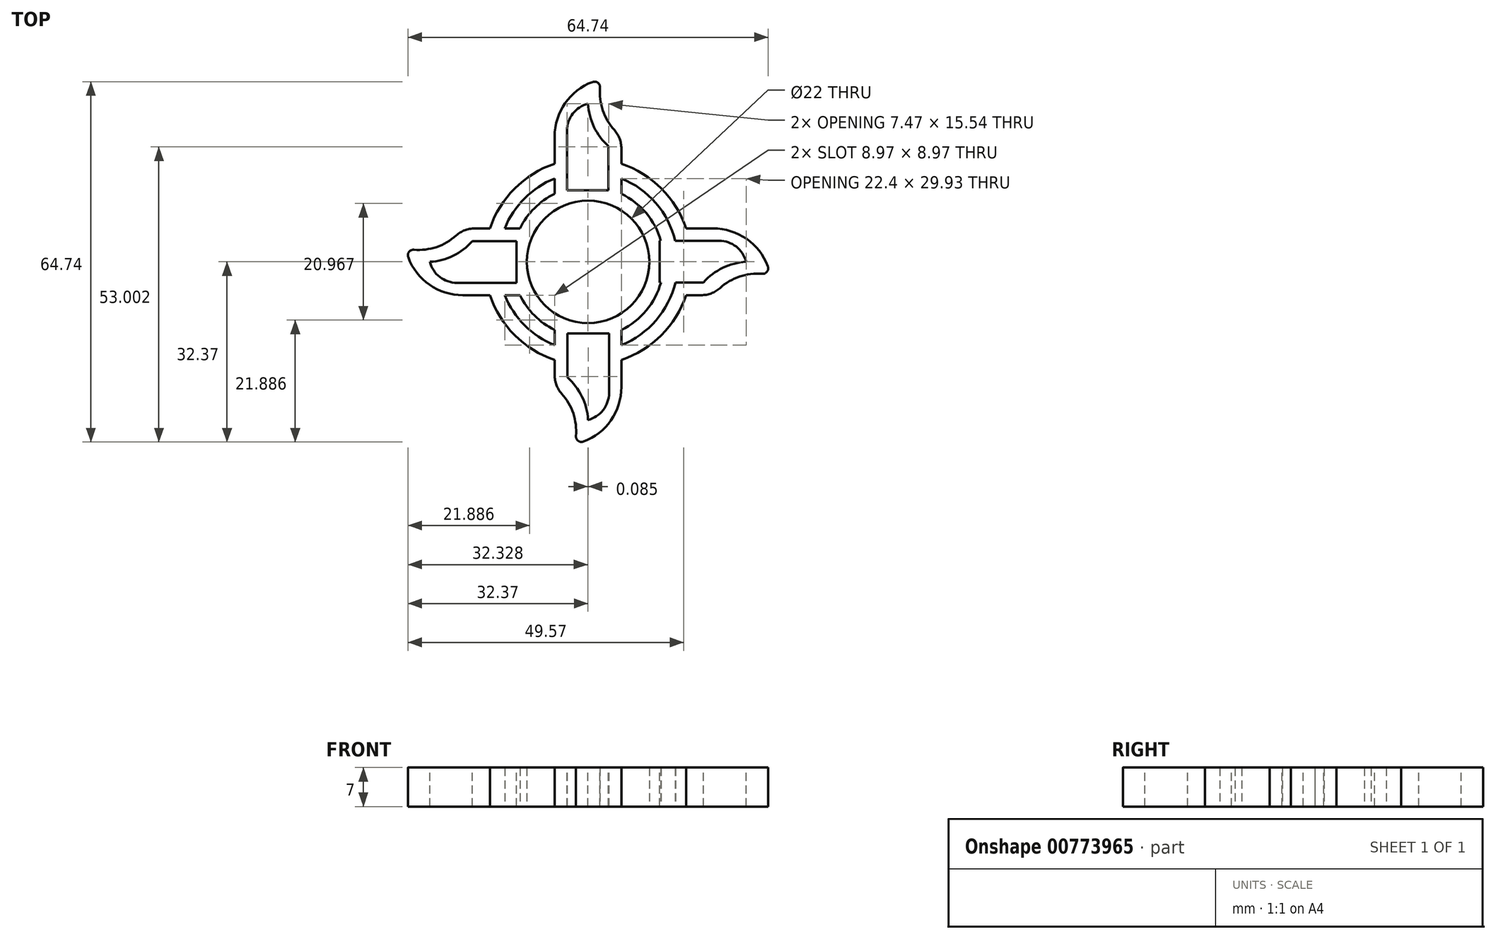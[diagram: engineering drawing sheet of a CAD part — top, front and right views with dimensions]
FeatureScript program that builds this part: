
annotation { "Feature Type Name" : "Feature", "Feature Type Description" : "" }
export const myFeature = defineFeature(function(context is Context, id is Id, definition is map)
    precondition{}
    {
        {
            var Q0;
            Q0=qCreatedBy(makeId("Top.planeOp"),FACE);
            var sketch = newSketch(context, id + "F0", { "sketchPlane" : qUnion([Q0])});
            skCircle(sketch, "E0", {"center": v(0, 0) * mm, "radius": 11 * mm});
            skLineSegment(sketch, "E1.bottom", {"start": v(-6, 22.5) * mm, "end": v(6, 22.5) * mm});
            skLineSegment(sketch, "E1.top", {"start": v(-6, -22.5) * mm, "end": v(6, -22.5) * mm});
            skLineSegment(sketch, "E1.left", {"start": v(-6, 22.5) * mm, "end": v(-6, -22.5) * mm});
            skLineSegment(sketch, "E1.right", {"start": v(6, 22.5) * mm, "end": v(6, -22.5) * mm});
            skLineSegment(sketch, "E2.bottom", {"start": v(-22.5, 6) * mm, "end": v(22.5, 6) * mm});
            skLineSegment(sketch, "E2.top", {"start": v(-22.5, -6) * mm, "end": v(22.5, -6) * mm});
            skLineSegment(sketch, "E2.left", {"start": v(-22.5, 6) * mm, "end": v(-22.5, -6) * mm});
            skLineSegment(sketch, "E2.right", {"start": v(22.5, 6) * mm, "end": v(22.5, -6) * mm});
            skCircle(sketch, "E3", {"center": v(0, 0) * mm, "radius": 13.62 * mm});
            skCircle(sketch, "E4", {"center": v(0, 0) * mm, "radius": 16.12 * mm});
            skCircle(sketch, "E5", {"center": v(0, 0) * mm, "radius": 18.62 * mm});
            skArc(sketch, "E6", {"start": v(2.4, 32.76) * mm, "mid": v(-3.63, 29.13) * mm, "end": v(-6, 22.5) * mm});
            skArc(sketch, "E7", {"start": v(2.4, 32.76) * mm, "mid": v(2.7, 27.1) * mm, "end": v(6, 22.5) * mm});
            skArc(sketch, "E8.1.0", {"start": v(-32.76, 2.4) * mm, "mid": v(-29.13, -3.63) * mm, "end": v(-22.5, -6) * mm});
            skArc(sketch, "E8.1.1", {"start": v(-32.76, 2.4) * mm, "mid": v(-27.1, 2.7) * mm, "end": v(-22.5, 6) * mm});
            skArc(sketch, "E8.2.0", {"start": v(-2.4, -32.76) * mm, "mid": v(3.63, -29.13) * mm, "end": v(6, -22.5) * mm});
            skArc(sketch, "E8.2.1", {"start": v(-2.4, -32.76) * mm, "mid": v(-2.7, -27.1) * mm, "end": v(-6, -22.5) * mm});
            skArc(sketch, "E8.3.0", {"start": v(32.76, -2.4) * mm, "mid": v(29.13, 3.63) * mm, "end": v(22.5, 6) * mm});
            skArc(sketch, "E8.3.1", {"start": v(32.76, -2.4) * mm, "mid": v(27.1, -2.7) * mm, "end": v(22.5, -6) * mm});
            skSolve(sketch);
        }
        {
            var Q0;
            Q0=qSketchRegion(id+"F0",true);
            var Q1;
            {var subQ0=sQuery(id+"F0.wireOp",EDGE,"6NycPAKA-UdFo-154e-vG3G-gpo5dTehrfDB");var subQ1=sQuery(id+"F0.wireOp",EDGE,"E1.left");var subQ2=makeQuery(id+"F0.imprint","INTERSECT",VERTEX,{"disambiguationData":[OD(0.0)],"derivedFrom":[subQ1,subQ0]});Q1=makeQuery(id+"F0.imprint","IMPRINT",FACE,{"disambiguationData":[TD([[makeQuery(id+"F0.imprint","IMPRINT",EDGE,{"disambiguationData":[TD([[subQ2,-1.0]])],"derivedFrom":subQ1}),1.0]])]});}
            var Q2;
            {var subQ0=sQuery(id+"F0.wireOp",EDGE,"bznZg16n-hZks-fmwa-Rq5P-ZMjDfiLHH9gW");var subQ1=sQuery(id+"F0.wireOp",EDGE,"E1.left");var subQ2=makeQuery(id+"F0.imprint","INTERSECT",VERTEX,{"disambiguationData":[OD(0.0)],"derivedFrom":[subQ1,subQ0]});Q2=makeQuery(id+"F0.imprint","IMPRINT",FACE,{"disambiguationData":[TD([[makeQuery(id+"F0.imprint","IMPRINT",EDGE,{"disambiguationData":[TD([[subQ2,-1.0]])],"derivedFrom":subQ1}),1.0]])]});}
            var Q3;
            {var subQ0=sQuery(id+"F0.wireOp",EDGE,"p4xlDRTD-oR5T-9qnb-qPoB-Fa0TsUWnMOog");var subQ1=sQuery(id+"F0.wireOp",EDGE,"E1.left");var subQ2=makeQuery(id+"F0.imprint","INTERSECT",VERTEX,{"disambiguationData":[OD(0.0)],"derivedFrom":[subQ1,subQ0]});Q3=makeQuery(id+"F0.imprint","IMPRINT",FACE,{"disambiguationData":[TD([[makeQuery(id+"F0.imprint","IMPRINT",EDGE,{"disambiguationData":[TD([[subQ2,-1.0]])],"derivedFrom":subQ1}),1.0]])]});}
            var Q4;
            {var subQ0=sQuery(id+"F0.wireOp",EDGE,"E5");var subQ1=sQuery(id+"F0.wireOp",EDGE,"E1.left");var subQ2=makeQuery(id+"F0.imprint","INTERSECT",VERTEX,{"disambiguationData":[OD(0.0)],"derivedFrom":[subQ1,subQ0]});Q4=makeQuery(id+"F0.imprint","IMPRINT",FACE,{"disambiguationData":[TD([[makeQuery(id+"F0.imprint","IMPRINT",EDGE,{"disambiguationData":[TD([[subQ2,-1.0]])],"derivedFrom":subQ1}),1.0]])]});}
            var Q5;
            {var subQ0=sQuery(id+"F0.wireOp",EDGE,"E4");var subQ1=sQuery(id+"F0.wireOp",EDGE,"E1.left");var subQ2=makeQuery(id+"F0.imprint","INTERSECT",VERTEX,{"disambiguationData":[OD(0.0)],"derivedFrom":[subQ1,subQ0]});Q5=makeQuery(id+"F0.imprint","IMPRINT",FACE,{"disambiguationData":[TD([[makeQuery(id+"F0.imprint","IMPRINT",EDGE,{"disambiguationData":[TD([[subQ2,-1.0]])],"derivedFrom":subQ1}),1.0]])]});}
            var Q6;
            {var subQ0=sQuery(id+"F0.wireOp",EDGE,"E1.right");var subQ1=sQuery(id+"F0.wireOp",EDGE,"E0");var subQ2=makeQuery(id+"F0.imprint","INTERSECT",VERTEX,{"disambiguationData":[OD(0.0)],"derivedFrom":[subQ1,subQ0]});Q6=makeQuery(id+"F0.imprint","IMPRINT",FACE,{"disambiguationData":[TD([[makeQuery(id+"F0.imprint","IMPRINT",EDGE,{"disambiguationData":[TD([[subQ2,-1.0]])],"derivedFrom":subQ1}),-1.0]])]});}
            var Q7;
            {var subQ0=sQuery(id+"F0.wireOp",EDGE,"6NycPAKA-UdFo-154e-vG3G-gpo5dTehrfDB");var subQ1=sQuery(id+"F0.wireOp",EDGE,"E2.bottom");var subQ2=makeQuery(id+"F0.imprint","INTERSECT",VERTEX,{"disambiguationData":[OD(0.0)],"derivedFrom":[subQ1,subQ0]});Q7=makeQuery(id+"F0.imprint","IMPRINT",FACE,{"disambiguationData":[TD([[makeQuery(id+"F0.imprint","IMPRINT",EDGE,{"disambiguationData":[TD([[subQ2,-1.0]])],"derivedFrom":subQ1}),-1.0]])]});}
            var Q8;
            {var subQ0=sQuery(id+"F0.wireOp",EDGE,"bznZg16n-hZks-fmwa-Rq5P-ZMjDfiLHH9gW");var subQ1=sQuery(id+"F0.wireOp",EDGE,"E2.bottom");var subQ2=makeQuery(id+"F0.imprint","INTERSECT",VERTEX,{"disambiguationData":[OD(0.0)],"derivedFrom":[subQ1,subQ0]});Q8=makeQuery(id+"F0.imprint","IMPRINT",FACE,{"disambiguationData":[TD([[makeQuery(id+"F0.imprint","IMPRINT",EDGE,{"disambiguationData":[TD([[subQ2,-1.0]])],"derivedFrom":subQ1}),-1.0]])]});}
            var Q9;
            {var subQ0=sQuery(id+"F0.wireOp",EDGE,"p4xlDRTD-oR5T-9qnb-qPoB-Fa0TsUWnMOog");var subQ1=sQuery(id+"F0.wireOp",EDGE,"E2.bottom");var subQ2=makeQuery(id+"F0.imprint","INTERSECT",VERTEX,{"disambiguationData":[OD(0.0)],"derivedFrom":[subQ1,subQ0]});Q9=makeQuery(id+"F0.imprint","IMPRINT",FACE,{"disambiguationData":[TD([[makeQuery(id+"F0.imprint","IMPRINT",EDGE,{"disambiguationData":[TD([[subQ2,-1.0]])],"derivedFrom":subQ1}),-1.0]])]});}
            var Q10;
            {var subQ0=sQuery(id+"F0.wireOp",EDGE,"E5");var subQ1=sQuery(id+"F0.wireOp",EDGE,"E2.bottom");var subQ2=makeQuery(id+"F0.imprint","INTERSECT",VERTEX,{"disambiguationData":[OD(0.0)],"derivedFrom":[subQ1,subQ0]});Q10=makeQuery(id+"F0.imprint","IMPRINT",FACE,{"disambiguationData":[TD([[makeQuery(id+"F0.imprint","IMPRINT",EDGE,{"disambiguationData":[TD([[subQ2,-1.0]])],"derivedFrom":subQ1}),-1.0]])]});}
            var Q11;
            {var subQ0=sQuery(id+"F0.wireOp",EDGE,"E4");var subQ1=sQuery(id+"F0.wireOp",EDGE,"E2.bottom");var subQ2=makeQuery(id+"F0.imprint","INTERSECT",VERTEX,{"disambiguationData":[OD(0.0)],"derivedFrom":[subQ1,subQ0]});Q11=makeQuery(id+"F0.imprint","IMPRINT",FACE,{"disambiguationData":[TD([[makeQuery(id+"F0.imprint","IMPRINT",EDGE,{"disambiguationData":[TD([[subQ2,-1.0]])],"derivedFrom":subQ1}),-1.0]])]});}
            var Q12;
            {var subQ0=sQuery(id+"F0.wireOp",EDGE,"E2.bottom");var subQ1=sQuery(id+"F0.wireOp",EDGE,"E0");var subQ2=makeQuery(id+"F0.imprint","INTERSECT",VERTEX,{"disambiguationData":[OD(1.0)],"derivedFrom":[subQ1,subQ0]});Q12=makeQuery(id+"F0.imprint","IMPRINT",FACE,{"disambiguationData":[TD([[makeQuery(id+"F0.imprint","IMPRINT",EDGE,{"disambiguationData":[TD([[subQ2,-1.0]])],"derivedFrom":subQ1}),-1.0]])]});}
            var Q13;
            {var subQ0=sQuery(id+"F0.wireOp",EDGE,"bznZg16n-hZks-fmwa-Rq5P-ZMjDfiLHH9gW");var subQ1=sQuery(id+"F0.wireOp",EDGE,"E2.bottom");var subQ2=makeQuery(id+"F0.imprint","INTERSECT",VERTEX,{"disambiguationData":[OD(1.0)],"derivedFrom":[subQ1,subQ0]});Q13=makeQuery(id+"F0.imprint","IMPRINT",FACE,{"disambiguationData":[TD([[makeQuery(id+"F0.imprint","IMPRINT",EDGE,{"disambiguationData":[TD([[subQ2,-1.0]])],"derivedFrom":subQ1}),-1.0]])]});}
            var Q14;
            {var subQ0=sQuery(id+"F0.wireOp",EDGE,"p4xlDRTD-oR5T-9qnb-qPoB-Fa0TsUWnMOog");var subQ1=sQuery(id+"F0.wireOp",EDGE,"E2.bottom");var subQ2=makeQuery(id+"F0.imprint","INTERSECT",VERTEX,{"disambiguationData":[OD(1.0)],"derivedFrom":[subQ1,subQ0]});Q14=makeQuery(id+"F0.imprint","IMPRINT",FACE,{"disambiguationData":[TD([[makeQuery(id+"F0.imprint","IMPRINT",EDGE,{"disambiguationData":[TD([[subQ2,-1.0]])],"derivedFrom":subQ1}),-1.0]])]});}
            var Q15;
            {var subQ0=sQuery(id+"F0.wireOp",EDGE,"E4");var subQ1=sQuery(id+"F0.wireOp",EDGE,"E2.bottom");var subQ2=makeQuery(id+"F0.imprint","INTERSECT",VERTEX,{"disambiguationData":[OD(1.0)],"derivedFrom":[subQ1,subQ0]});Q15=makeQuery(id+"F0.imprint","IMPRINT",FACE,{"disambiguationData":[TD([[makeQuery(id+"F0.imprint","IMPRINT",EDGE,{"disambiguationData":[TD([[subQ2,-1.0]])],"derivedFrom":subQ1}),-1.0]])]});}
            var Q16;
            {var subQ0=sQuery(id+"F0.wireOp",EDGE,"E3");var subQ1=sQuery(id+"F0.wireOp",EDGE,"E2.bottom");var subQ2=makeQuery(id+"F0.imprint","INTERSECT",VERTEX,{"disambiguationData":[OD(1.0)],"derivedFrom":[subQ1,subQ0]});Q16=makeQuery(id+"F0.imprint","IMPRINT",FACE,{"disambiguationData":[TD([[makeQuery(id+"F0.imprint","IMPRINT",EDGE,{"disambiguationData":[TD([[subQ2,-1.0]])],"derivedFrom":subQ1}),-1.0]])]});}
            var Q17;
            {var subQ0=sQuery(id+"F0.wireOp",EDGE,"E2.bottom");var subQ1=sQuery(id+"F0.wireOp",EDGE,"E0");var subQ2=makeQuery(id+"F0.imprint","INTERSECT",VERTEX,{"disambiguationData":[OD(0.0)],"derivedFrom":[subQ1,subQ0]});Q17=makeQuery(id+"F0.imprint","IMPRINT",FACE,{"disambiguationData":[TD([[makeQuery(id+"F0.imprint","IMPRINT",EDGE,{"disambiguationData":[TD([[subQ2,1.0]])],"derivedFrom":subQ1}),-1.0]])]});}
            var Q18;
            {var subQ0=sQuery(id+"F0.wireOp",EDGE,"E5");var subQ1=sQuery(id+"F0.wireOp",EDGE,"E1.left");var subQ2=makeQuery(id+"F0.imprint","INTERSECT",VERTEX,{"disambiguationData":[OD(1.0)],"derivedFrom":[subQ1,subQ0]});Q18=makeQuery(id+"F0.imprint","IMPRINT",FACE,{"disambiguationData":[TD([[makeQuery(id+"F0.imprint","IMPRINT",EDGE,{"disambiguationData":[TD([[subQ2,-1.0]])],"derivedFrom":subQ1}),1.0]])]});}
            var Q19;
            {var subQ0=sQuery(id+"F0.wireOp",EDGE,"p4xlDRTD-oR5T-9qnb-qPoB-Fa0TsUWnMOog");var subQ1=sQuery(id+"F0.wireOp",EDGE,"E1.left");var subQ2=makeQuery(id+"F0.imprint","INTERSECT",VERTEX,{"disambiguationData":[OD(1.0)],"derivedFrom":[subQ1,subQ0]});Q19=makeQuery(id+"F0.imprint","IMPRINT",FACE,{"disambiguationData":[TD([[makeQuery(id+"F0.imprint","IMPRINT",EDGE,{"disambiguationData":[TD([[subQ2,-1.0]])],"derivedFrom":subQ1}),1.0]])]});}
            var Q20;
            {var subQ0=sQuery(id+"F0.wireOp",EDGE,"bznZg16n-hZks-fmwa-Rq5P-ZMjDfiLHH9gW");var subQ1=sQuery(id+"F0.wireOp",EDGE,"E1.left");var subQ2=makeQuery(id+"F0.imprint","INTERSECT",VERTEX,{"disambiguationData":[OD(1.0)],"derivedFrom":[subQ1,subQ0]});Q20=makeQuery(id+"F0.imprint","IMPRINT",FACE,{"disambiguationData":[TD([[makeQuery(id+"F0.imprint","IMPRINT",EDGE,{"disambiguationData":[TD([[subQ2,-1.0]])],"derivedFrom":subQ1}),1.0]])]});}
            var Q21;
            {var subQ0=sQuery(id+"F0.wireOp",EDGE,"E4");var subQ1=sQuery(id+"F0.wireOp",EDGE,"E1.left");var subQ2=makeQuery(id+"F0.imprint","INTERSECT",VERTEX,{"disambiguationData":[OD(1.0)],"derivedFrom":[subQ1,subQ0]});Q21=makeQuery(id+"F0.imprint","IMPRINT",FACE,{"disambiguationData":[TD([[makeQuery(id+"F0.imprint","IMPRINT",EDGE,{"disambiguationData":[TD([[subQ2,-1.0]])],"derivedFrom":subQ1}),1.0]])]});}
            var Q22;
            {var subQ0=sQuery(id+"F0.wireOp",EDGE,"E3");var subQ1=sQuery(id+"F0.wireOp",EDGE,"E1.left");var subQ2=makeQuery(id+"F0.imprint","INTERSECT",VERTEX,{"disambiguationData":[OD(1.0)],"derivedFrom":[subQ1,subQ0]});Q22=makeQuery(id+"F0.imprint","IMPRINT",FACE,{"disambiguationData":[TD([[makeQuery(id+"F0.imprint","IMPRINT",EDGE,{"disambiguationData":[TD([[subQ2,-1.0]])],"derivedFrom":subQ1}),1.0]])]});}
            var Q23;
            {var subQ0=sQuery(id+"F0.wireOp",EDGE,"E1.left");var subQ1=sQuery(id+"F0.wireOp",EDGE,"E0");var subQ2=makeQuery(id+"F0.imprint","INTERSECT",VERTEX,{"disambiguationData":[OD(1.0)],"derivedFrom":[subQ1,subQ0]});Q23=makeQuery(id+"F0.imprint","IMPRINT",FACE,{"disambiguationData":[TD([[makeQuery(id+"F0.imprint","IMPRINT",EDGE,{"disambiguationData":[TD([[subQ2,-1.0]])],"derivedFrom":subQ1}),-1.0]])]});}
            var Q24;
            {var subQ0=sQuery(id+"F0.wireOp",EDGE,"E5");var subQ1=sQuery(id+"F0.wireOp",EDGE,"E2.bottom");var subQ2=makeQuery(id+"F0.imprint","INTERSECT",VERTEX,{"disambiguationData":[OD(1.0)],"derivedFrom":[subQ1,subQ0]});Q24=makeQuery(id+"F0.imprint","IMPRINT",FACE,{"disambiguationData":[TD([[makeQuery(id+"F0.imprint","IMPRINT",EDGE,{"disambiguationData":[TD([[subQ2,-1.0]])],"derivedFrom":subQ1}),-1.0]])]});}
            var Q25;
            {var subQ0=sQuery(id+"F0.wireOp",EDGE,"E1.left");var subQ1=sQuery(id+"F0.wireOp",EDGE,"E0");var subQ2=makeQuery(id+"F0.imprint","INTERSECT",VERTEX,{"disambiguationData":[OD(0.0)],"derivedFrom":[subQ1,subQ0]});Q25=makeQuery(id+"F0.imprint","IMPRINT",FACE,{"disambiguationData":[TD([[makeQuery(id+"F0.imprint","IMPRINT",EDGE,{"disambiguationData":[TD([[subQ2,-1.0]])],"derivedFrom":subQ1}),-1.0]])]});}
            var Q26;
            {var subQ0=sQuery(id+"F0.wireOp",EDGE,"E1.right");var subQ1=sQuery(id+"F0.wireOp",EDGE,"E0");var subQ2=makeQuery(id+"F0.imprint","INTERSECT",VERTEX,{"disambiguationData":[OD(0.0)],"derivedFrom":[subQ1,subQ0]});Q26=makeQuery(id+"F0.imprint","IMPRINT",FACE,{"disambiguationData":[TD([[makeQuery(id+"F0.imprint","IMPRINT",EDGE,{"disambiguationData":[TD([[subQ2,1.0]])],"derivedFrom":subQ1}),-1.0]])]});}
            var Q27;
            {var subQ0=sQuery(id+"F0.wireOp",EDGE,"E1.right");var subQ1=sQuery(id+"F0.wireOp",EDGE,"E0");var subQ2=makeQuery(id+"F0.imprint","INTERSECT",VERTEX,{"disambiguationData":[OD(1.0)],"derivedFrom":[subQ1,subQ0]});Q27=makeQuery(id+"F0.imprint","IMPRINT",FACE,{"disambiguationData":[TD([[makeQuery(id+"F0.imprint","IMPRINT",EDGE,{"disambiguationData":[TD([[subQ2,-1.0]])],"derivedFrom":subQ1}),-1.0]])]});}
            var Q28;
            {var subQ0=sQuery(id+"F0.wireOp",EDGE,"E2.top");var subQ1=sQuery(id+"F0.wireOp",EDGE,"E0");var subQ2=makeQuery(id+"F0.imprint","INTERSECT",VERTEX,{"disambiguationData":[OD(0.0)],"derivedFrom":[subQ1,subQ0]});Q28=makeQuery(id+"F0.imprint","IMPRINT",FACE,{"disambiguationData":[TD([[makeQuery(id+"F0.imprint","IMPRINT",EDGE,{"disambiguationData":[TD([[subQ2,-1.0]])],"derivedFrom":subQ1}),-1.0]])]});}
            var Q29;
            {var subQ0=sQuery(id+"F0.wireOp",EDGE,"E4");var subQ1=sQuery(id+"F0.wireOp",EDGE,"E1.left");var subQ2=makeQuery(id+"F0.imprint","INTERSECT",VERTEX,{"disambiguationData":[OD(1.0)],"derivedFrom":[subQ1,subQ0]});Q29=makeQuery(id+"F0.imprint","IMPRINT",FACE,{"disambiguationData":[TD([[makeQuery(id+"F0.imprint","IMPRINT",EDGE,{"disambiguationData":[TD([[subQ2,-1.0]])],"derivedFrom":subQ1}),-1.0]])]});}
            var Q30;
            {var subQ0=sQuery(id+"F0.wireOp",EDGE,"E4");var subQ1=sQuery(id+"F0.wireOp",EDGE,"E1.right");var subQ2=makeQuery(id+"F0.imprint","INTERSECT",VERTEX,{"disambiguationData":[OD(1.0)],"derivedFrom":[subQ1,subQ0]});Q30=makeQuery(id+"F0.imprint","IMPRINT",FACE,{"disambiguationData":[TD([[makeQuery(id+"F0.imprint","IMPRINT",EDGE,{"disambiguationData":[TD([[subQ2,-1.0]])],"derivedFrom":subQ1}),1.0]])]});}
            var Q31;
            {var subQ0=sQuery(id+"F0.wireOp",EDGE,"E5");var subQ1=sQuery(id+"F0.wireOp",EDGE,"E1.right");var subQ2=makeQuery(id+"F0.imprint","INTERSECT",VERTEX,{"disambiguationData":[OD(0.0)],"derivedFrom":[subQ1,subQ0]});Q31=makeQuery(id+"F0.imprint","IMPRINT",FACE,{"disambiguationData":[TD([[makeQuery(id+"F0.imprint","IMPRINT",EDGE,{"disambiguationData":[TD([[subQ2,-1.0]])],"derivedFrom":subQ1}),1.0]])]});}
            var Q32;
            {var subQ0=sQuery(id+"F0.wireOp",EDGE,"E5");var subQ1=sQuery(id+"F0.wireOp",EDGE,"E1.left");var subQ2=makeQuery(id+"F0.imprint","INTERSECT",VERTEX,{"disambiguationData":[OD(0.0)],"derivedFrom":[subQ1,subQ0]});Q32=makeQuery(id+"F0.imprint","IMPRINT",FACE,{"disambiguationData":[TD([[makeQuery(id+"F0.imprint","IMPRINT",EDGE,{"disambiguationData":[TD([[subQ2,-1.0]])],"derivedFrom":subQ1}),-1.0]])]});}
            var Q33;
            {var subQ0=sQuery(id+"F0.wireOp",EDGE,"bznZg16n-hZks-fmwa-Rq5P-ZMjDfiLHH9gW");var subQ1=sQuery(id+"F0.wireOp",EDGE,"E1.left");var subQ2=makeQuery(id+"F0.imprint","INTERSECT",VERTEX,{"disambiguationData":[OD(0.0)],"derivedFrom":[subQ1,subQ0]});Q33=makeQuery(id+"F0.imprint","IMPRINT",FACE,{"disambiguationData":[TD([[makeQuery(id+"F0.imprint","IMPRINT",EDGE,{"disambiguationData":[TD([[subQ2,-1.0]])],"derivedFrom":subQ1}),-1.0]])]});}
            var Q34;
            {var subQ0=sQuery(id+"F0.wireOp",EDGE,"bznZg16n-hZks-fmwa-Rq5P-ZMjDfiLHH9gW");var subQ1=sQuery(id+"F0.wireOp",EDGE,"E1.right");var subQ2=makeQuery(id+"F0.imprint","INTERSECT",VERTEX,{"disambiguationData":[OD(0.0)],"derivedFrom":[subQ1,subQ0]});Q34=makeQuery(id+"F0.imprint","IMPRINT",FACE,{"disambiguationData":[TD([[makeQuery(id+"F0.imprint","IMPRINT",EDGE,{"disambiguationData":[TD([[subQ2,-1.0]])],"derivedFrom":subQ1}),1.0]])]});}
            var Q35;
            {var subQ0=sQuery(id+"F0.wireOp",EDGE,"p4xlDRTD-oR5T-9qnb-qPoB-Fa0TsUWnMOog");var subQ1=sQuery(id+"F0.wireOp",EDGE,"E1.right");var subQ2=makeQuery(id+"F0.imprint","INTERSECT",VERTEX,{"disambiguationData":[OD(1.0)],"derivedFrom":[subQ1,subQ0]});Q35=makeQuery(id+"F0.imprint","IMPRINT",FACE,{"disambiguationData":[TD([[makeQuery(id+"F0.imprint","IMPRINT",EDGE,{"disambiguationData":[TD([[subQ2,-1.0]])],"derivedFrom":subQ1}),1.0]])]});}
            var Q36;
            {var subQ0=sQuery(id+"F0.wireOp",EDGE,"p4xlDRTD-oR5T-9qnb-qPoB-Fa0TsUWnMOog");var subQ1=sQuery(id+"F0.wireOp",EDGE,"E1.left");var subQ2=makeQuery(id+"F0.imprint","INTERSECT",VERTEX,{"disambiguationData":[OD(1.0)],"derivedFrom":[subQ1,subQ0]});Q36=makeQuery(id+"F0.imprint","IMPRINT",FACE,{"disambiguationData":[TD([[makeQuery(id+"F0.imprint","IMPRINT",EDGE,{"disambiguationData":[TD([[subQ2,-1.0]])],"derivedFrom":subQ1}),-1.0]])]});}
            extrude(context, id + "F1", {"entities" : qUnion([Q0, Q1, Q2, Q3, Q4, Q5, Q6, Q7, Q8, Q9, Q10, Q11, Q12, Q13, Q14, Q15, Q16, Q17, Q18, Q19, Q20, Q21, Q22, Q23, Q24, Q25, Q26, Q27, Q28, Q29, Q30, Q31, Q32, Q33, Q34, Q35, Q36]), "depth" : 7 * mm, "offsetDistance" : 25 * mm});
        }
        {
            var Q0;
            Q0=makeQuery(id+"F1.opExtrude","SWEPT_EDGE",EDGE,{"disambiguationData":[OSD([sQuery(id+"F0.wireOp",EDGE,"E8.2.0"),sQuery(id+"F0.wireOp",EDGE,"E8.2.1")])]});
            var Q1;
            Q1=makeQuery(id+"F1.opExtrude","SWEPT_EDGE",EDGE,{"disambiguationData":[OSD([sQuery(id+"F0.wireOp",EDGE,"E8.1.0"),sQuery(id+"F0.wireOp",EDGE,"E8.1.1")])]});
            var Q2;
            Q2=makeQuery(id+"F1.opExtrude","SWEPT_EDGE",EDGE,{"disambiguationData":[OSD([sQuery(id+"F0.wireOp",EDGE,"E8.3.0"),sQuery(id+"F0.wireOp",EDGE,"E8.3.1")])]});
            var Q3;
            Q3=makeQuery(id+"F1.opExtrude","SWEPT_EDGE",EDGE,{"disambiguationData":[OSD([sQuery(id+"F0.wireOp",EDGE,"E6"),sQuery(id+"F0.wireOp",EDGE,"E7")])]});
            fillet(context, id + "F2", {"entities" : qUnion([Q0, Q1, Q2, Q3]), "radius" : 1 * mm, "tangentPropagation" : true, "allowEdgeOverflow" : false});
        }
        {
            var Q0;
            Q0=makeQuery(id+"F1.opExtrude","SWEPT_EDGE",EDGE,{"disambiguationData":[OSD([sQuery(id+"F0.wireOp",EDGE,"E2.bottom"),sQuery(id+"F0.wireOp",EDGE,"E2.left"),sQuery(id+"F0.wireOp",EDGE,"E8.1.1")])]});
            var Q1;
            Q1=makeQuery(id+"F1.opExtrude","SWEPT_EDGE",EDGE,{"disambiguationData":[OSD([sQuery(id+"F0.wireOp",EDGE,"E1.bottom"),sQuery(id+"F0.wireOp",EDGE,"E1.right"),sQuery(id+"F0.wireOp",EDGE,"E7")])]});
            var Q2;
            Q2=makeQuery(id+"F1.opExtrude","SWEPT_EDGE",EDGE,{"disambiguationData":[OSD([sQuery(id+"F0.wireOp",EDGE,"E2.top"),sQuery(id+"F0.wireOp",EDGE,"E2.right"),sQuery(id+"F0.wireOp",EDGE,"E8.3.1")])]});
            var Q3;
            Q3=makeQuery(id+"F1.opExtrude","SWEPT_EDGE",EDGE,{"disambiguationData":[OSD([sQuery(id+"F0.wireOp",EDGE,"E1.top"),sQuery(id+"F0.wireOp",EDGE,"E1.left"),sQuery(id+"F0.wireOp",EDGE,"E8.2.1")])]});
            fillet(context, id + "F3", {"entities" : qUnion([Q0, Q1, Q2, Q3]), "radius" : 5 * mm, "tangentPropagation" : true, "allowEdgeOverflow" : false});
        }
        {
            var Q0;
            Q0=makeQuery(id+"F1.opExtrude","CAP_FACE",FACE,{"disambiguationData":[OSD([sQuery(id+"F0.wireOp",EDGE,"E0"),sQuery(id+"F0.wireOp",EDGE,"E1.left"),sQuery(id+"F0.wireOp",EDGE,"E1.right"),sQuery(id+"F0.wireOp",EDGE,"E2.bottom"),sQuery(id+"F0.wireOp",EDGE,"E2.top"),sQuery(id+"F0.wireOp",EDGE,"E3"),sQuery(id+"F0.wireOp",EDGE,"E4"),sQuery(id+"F0.wireOp",EDGE,"E5"),sQuery(id+"F0.wireOp",EDGE,"E6"),sQuery(id+"F0.wireOp",EDGE,"E7"),sQuery(id+"F0.wireOp",EDGE,"E8.1.0"),sQuery(id+"F0.wireOp",EDGE,"E8.1.1"),sQuery(id+"F0.wireOp",EDGE,"E8.2.0"),sQuery(id+"F0.wireOp",EDGE,"E8.2.1"),sQuery(id+"F0.wireOp",EDGE,"E8.3.0"),sQuery(id+"F0.wireOp",EDGE,"E8.3.1")])],"isStart":false});
            var sketch = newSketch(context, id + "F4", { "sketchPlane" : qUnion([Q0])});
            skLineSegment(sketch, "E9", {"start": v(-3.78, 23.56) * mm, "end": v(-3.78, 12.86) * mm});
            skLineSegment(sketch, "E10", {"start": v(-3.78, 12.86) * mm, "end": v(3.7, 12.86) * mm});
            skLineSegment(sketch, "E11", {"start": v(3.7, 12.86) * mm, "end": v(3.7, 20.76) * mm});
            skArc(sketch, "E12", {"start": v(0, 28.4) * mm, "mid": v(-2.72, 26.63) * mm, "end": v(-3.78, 23.56) * mm});
            skArc(sketch, "E13", {"start": v(0, 28.4) * mm, "mid": v(1.08, 24.21) * mm, "end": v(3.7, 20.76) * mm});
            skArc(sketch, "E14.1.0", {"start": v(-28.4, 0) * mm, "mid": v(-26.63, -2.72) * mm, "end": v(-23.56, -3.78) * mm});
            skArc(sketch, "E14.1.1", {"start": v(-28.4, 0) * mm, "mid": v(-24.21, 1.08) * mm, "end": v(-20.76, 3.7) * mm});
            skLineSegment(sketch, "E14.1.2", {"start": v(-23.56, -3.78) * mm, "end": v(-12.86, -3.78) * mm});
            skLineSegment(sketch, "E14.1.3", {"start": v(-12.86, 3.7) * mm, "end": v(-20.76, 3.7) * mm});
            skLineSegment(sketch, "E14.1.4", {"start": v(-12.86, -3.78) * mm, "end": v(-12.86, 3.7) * mm});
            skArc(sketch, "E14.2.0", {"start": v(0, -28.4) * mm, "mid": v(2.72, -26.63) * mm, "end": v(3.78, -23.56) * mm});
            skArc(sketch, "E14.2.1", {"start": v(0, -28.4) * mm, "mid": v(-1.08, -24.21) * mm, "end": v(-3.7, -20.76) * mm});
            skLineSegment(sketch, "E14.2.2", {"start": v(3.78, -23.56) * mm, "end": v(3.78, -12.86) * mm});
            skLineSegment(sketch, "E14.2.3", {"start": v(-3.7, -12.86) * mm, "end": v(-3.7, -20.76) * mm});
            skLineSegment(sketch, "E14.2.4", {"start": v(3.78, -12.86) * mm, "end": v(-3.7, -12.86) * mm});
            skArc(sketch, "E14.3.0", {"start": v(28.4, 0) * mm, "mid": v(26.63, 2.72) * mm, "end": v(23.56, 3.78) * mm});
            skArc(sketch, "E14.3.1", {"start": v(28.4, 0) * mm, "mid": v(24.21, -1.08) * mm, "end": v(20.76, -3.7) * mm});
            skLineSegment(sketch, "E14.3.2", {"start": v(23.56, 3.78) * mm, "end": v(12.86, 3.78) * mm});
            skLineSegment(sketch, "E14.3.3", {"start": v(12.86, -3.7) * mm, "end": v(20.76, -3.7) * mm});
            skLineSegment(sketch, "E14.3.4", {"start": v(12.86, 3.78) * mm, "end": v(12.86, -3.7) * mm});
            skPoint(sketch, "E14.center", {"position": v(0, 0) * mm});
            skSolve(sketch);
        }
        {
            var Q0;
            Q0=qSketchRegion(id+"F4",true);
            extrude(context, id + "F5", {"entities" : qUnion([Q0]), "operationType" : NewBodyOperationType.REMOVE, "oppositeDirection" : true, "depth" : 25 * mm, "offsetDistance" : 25 * mm});
        }
    });
